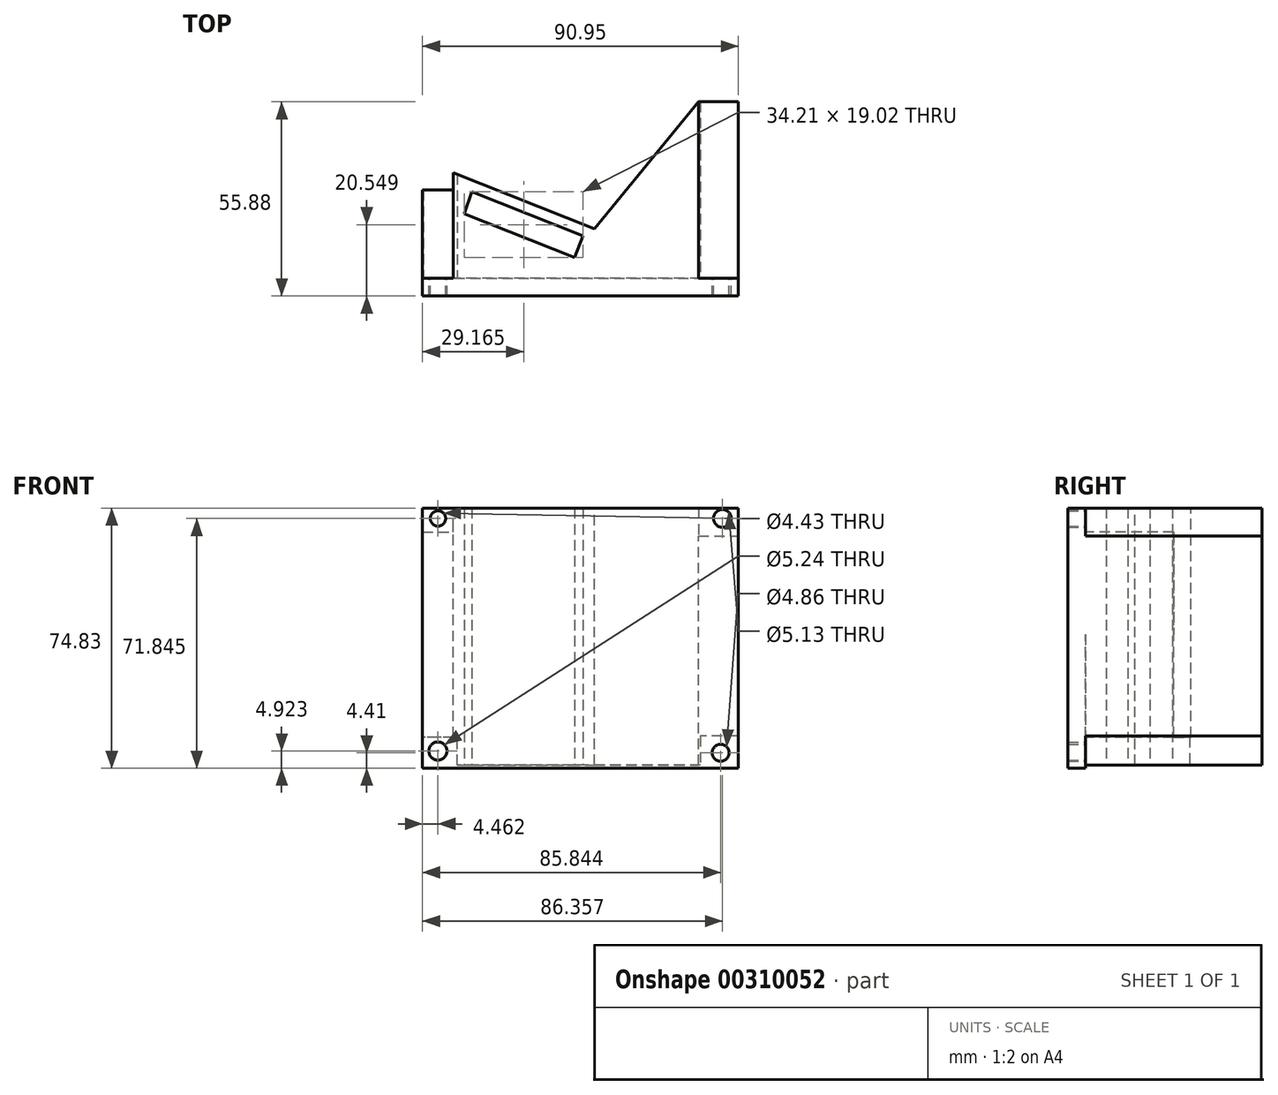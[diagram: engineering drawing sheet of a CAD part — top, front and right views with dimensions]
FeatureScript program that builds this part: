
annotation { "Feature Type Name" : "Feature", "Feature Type Description" : "" }
export const myFeature = defineFeature(function(context is Context, id is Id, definition is map)
    precondition{}
    {
        {
            var Q0;
            Q0=qCreatedBy(makeId("Front.planeOp"),FACE);
            var sketch = newSketch(context, id + "F0", { "sketchPlane" : qUnion([Q0])});
            skLineSegment(sketch, "E0.bottom", {"start": v(-36.84, 39.14) * mm, "end": v(54.1, 39.14) * mm});
            skLineSegment(sketch, "E0.top", {"start": v(-36.84, -35.69) * mm, "end": v(54.1, -35.69) * mm});
            skLineSegment(sketch, "E0.left", {"start": v(-36.84, 39.14) * mm, "end": v(-36.84, -35.69) * mm});
            skLineSegment(sketch, "E0.right", {"start": v(54.1, 39.14) * mm, "end": v(54.1, -35.69) * mm});
            skSolve(sketch);
        }
        {
            var Q0;
            Q0=makeQuery(id+"F0.imprint","IMPRINT",FACE,{"disambiguationData":[TD([[makeQuery(id+"F0.imprint","IMPRINT",EDGE,{"derivedFrom":sQuery(id+"F0.wireOp",EDGE,"E0.bottom")}),-1.0]])]});
            var sketch = newSketch(context, id + "F1", { "sketchPlane" : qUnion([Q0])});
            skLineSegment(sketch, "E1", {"start": v(-37.13, 32.23) * mm, "end": v(-27.92, 32.23) * mm});
            skLineSegment(sketch, "E2", {"start": v(-27.92, 32.23) * mm, "end": v(-27.92, 39.14) * mm});
            skLineSegment(sketch, "E3", {"start": v(-27.92, 39.14) * mm, "end": v(42.6, 39.14) * mm});
            skLineSegment(sketch, "E4", {"start": v(42.6, 39.14) * mm, "end": v(42.6, 31.08) * mm});
            skLineSegment(sketch, "E5", {"start": v(42.6, 31.08) * mm, "end": v(54.68, 31.08) * mm});
            skLineSegment(sketch, "E6", {"start": v(54.68, 31.08) * mm, "end": v(54.68, -26.48) * mm});
            skLineSegment(sketch, "E7", {"start": v(54.68, -26.48) * mm, "end": v(43.17, -26.48) * mm});
            skLineSegment(sketch, "E8", {"start": v(43.17, -26.48) * mm, "end": v(43.17, -34.82) * mm});
            skLineSegment(sketch, "E9", {"start": v(43.17, -34.82) * mm, "end": v(-26.77, -34.82) * mm});
            skLineSegment(sketch, "E10", {"start": v(-26.77, -34.82) * mm, "end": v(-26.77, -26.77) * mm});
            skLineSegment(sketch, "E11", {"start": v(-26.77, -26.77) * mm, "end": v(-36.55, -26.77) * mm});
            skLineSegment(sketch, "E12", {"start": v(-36.55, -26.77) * mm, "end": v(-37.13, 32.23) * mm});
            skSolve(sketch);
        }
        {
            var Q0;
            Q0=makeQuery(id+"F0.imprint","IMPRINT",FACE,{"disambiguationData":[TD([[makeQuery(id+"F0.imprint","IMPRINT",EDGE,{"derivedFrom":sQuery(id+"F0.wireOp",EDGE,"E0.bottom")}),-1.0]])]});
            extrude(context, id + "F2", {"entities" : qUnion([Q0]), "depth" : 5.08 * mm});
        }
        {
            var Q0;
            {var subQ7=sQuery(id+"F1.wireOp",EDGE,"E2");Q0=makeQuery(id+"F1.imprint","IMPRINT",FACE,{"disambiguationData":[TD([[makeQuery(id+"F1.imprint","IMPRINT",EDGE,{"derivedFrom":subQ7}),-1.0]])]});}
            extrude(context, id + "F3", {"entities" : qUnion([Q0]), "operationType" : NewBodyOperationType.ADD, "oppositeDirection" : true, "depth" : 50.8 * mm});
        }
        {
            var Q0;
            Q0=makeQuery(id+"F3.boolean.opBoolean","MERGE",FACE,{"derivedFrom":[makeQuery(id+"F2.opExtrude","SWEPT_FACE",FACE,{"disambiguationData":[OSD([sQuery(id+"F0.wireOp",EDGE,"E0.bottom")])]}),makeQuery(id+"F3.opExtrude","SWEPT_FACE",FACE,{"disambiguationData":[OSD([sQuery(id+"F1.wireOp",EDGE,"E3")])]})]});
            var sketch = newSketch(context, id + "F4", { "sketchPlane" : qUnion([Q0])});
            skLineSegment(sketch, "E13", {"start": v(-27.92, 30.39) * mm, "end": v(12.66, 14.23) * mm});
            skLineSegment(sketch, "E14", {"start": v(12.66, 14.23) * mm, "end": v(42.6, 50.8) * mm});
            skSolve(sketch);
        }
        {
            var Q0;
            {var subQ0=sQuery(id+"F4.wireOp",EDGE,"E13");Q0=makeQuery(id+"F4.imprint","IMPRINT",FACE,{"disambiguationData":[TD([[makeQuery(id+"F4.imprint","IMPRINT",EDGE,{"derivedFrom":subQ0}),1.0]])]});}
            extrude(context, id + "F5", {"entities" : qUnion([Q0]), "operationType" : NewBodyOperationType.REMOVE, "oppositeDirection" : true, "depth" : 76.2 * mm});
        }
        {
            var Q0;
            {var subQ0=sQuery(id+"F1.wireOp",EDGE,"E12");var subQ1=sQuery(id+"F1.wireOp",EDGE,"E11");var subQ2=sQuery(id+"F1.wireOp",EDGE,"E1");var subQ3=sQuery(id+"F0.wireOp",EDGE,"E0.left");var subQ4=sQuery(id+"F1.wireOp",EDGE,"E3");var subQ5=sQuery(id+"F1.wireOp",EDGE,"E2");Q0=makeQuery(id+"F5.boolean.opBoolean","SPLIT",FACE,{"disambiguationData":[TD([makeQuery(id+"F2.opExtrude","SWEPT_FACE",FACE,{"disambiguationData":[OSD([subQ3])]})])],"derivedFrom":makeQuery(id+"F3.opExtrude","CAP_FACE",FACE,{"disambiguationData":[OSD([subQ3,sQuery(id+"F0.wireOp",EDGE,"E0.right"),subQ2,subQ5,subQ4,sQuery(id+"F1.wireOp",EDGE,"E4"),sQuery(id+"F1.wireOp",EDGE,"E5"),sQuery(id+"F1.wireOp",EDGE,"E7"),sQuery(id+"F1.wireOp",EDGE,"E8"),sQuery(id+"F1.wireOp",EDGE,"E9"),sQuery(id+"F1.wireOp",EDGE,"E10"),subQ1,subQ0])],"isStart":false})});}
            extrude(context, id + "F6", {"entities" : qUnion([Q0]), "operationType" : NewBodyOperationType.REMOVE, "oppositeDirection" : true, "depth" : 25.4 * mm});
        }
        {
            var Q0;
            Q0=makeQuery(id+"F3.opExtrude","SWEPT_FACE",FACE,{"disambiguationData":[OSD([sQuery(id+"F1.wireOp",EDGE,"E9")])]});
            var sketch = newSketch(context, id + "F7", { "sketchPlane" : qUnion([Q0])});
            skLineSegment(sketch, "E15", {"start": v(-22.67, -24.98) * mm, "end": v(9.43, -12.2) * mm});
            skLineSegment(sketch, "E16", {"start": v(9.43, -12.2) * mm, "end": v(6.95, -5.96) * mm});
            skLineSegment(sketch, "E17", {"start": v(6.95, -5.96) * mm, "end": v(-24.78, -18.59) * mm});
            skPoint(sketch, "E17.endSnap0", {"position": v(-6.62, -18.59) * mm});
            skLineSegment(sketch, "E18", {"start": v(-24.78, -18.59) * mm, "end": v(-22.67, -24.98) * mm});
            skSolve(sketch);
        }
        {
            var Q0;
            Q0=makeQuery(id+"F7.imprint","IMPRINT",FACE,{"disambiguationData":[TD([[makeQuery(id+"F7.imprint","IMPRINT",EDGE,{"derivedFrom":sQuery(id+"F7.wireOp",EDGE,"E15")}),1.0]])]});
            extrude(context, id + "F8", {"entities" : qUnion([Q0]), "operationType" : NewBodyOperationType.REMOVE, "oppositeDirection" : true, "depth" : 101.6 * mm});
        }
        {
            var Q0;
            {var subQ0=sQuery(id+"F0.wireOp",EDGE,"E0.left");var subQ1=sQuery(id+"F0.wireOp",EDGE,"E0.bottom");Q0=makeQuery(id+"F3.boolean.opBoolean","SPLIT",FACE,{"disambiguationData":[TD([makeQuery(id+"F3.opExtrude","SWEPT_FACE",FACE,{"disambiguationData":[OSD([sQuery(id+"F1.wireOp",EDGE,"E1")])]})])],"derivedFrom":makeQuery(id+"F2.opExtrude","CAP_FACE",FACE,{"disambiguationData":[OSD([subQ1,sQuery(id+"F0.wireOp",EDGE,"E0.top"),subQ0,sQuery(id+"F0.wireOp",EDGE,"E0.right")])],"isStart":true})});}
            var sketch = newSketch(context, id + "F9", { "sketchPlane" : qUnion([Q0])});
            skCircle(sketch, "E19", {"center": v(32.38, 36.16) * mm, "radius": 2.21 * mm});
            skPoint(sketch, "E19.centerSnap0", {"position": v(32.38, 32.23) * mm});
            skCircle(sketch, "E20", {"center": v(32.38, -30.77) * mm, "radius": 2.62 * mm});
            skCircle(sketch, "E21", {"center": v(-49.52, 36.16) * mm, "radius": 2.56 * mm});
            skCircle(sketch, "E22", {"center": v(-49, -31.28) * mm, "radius": 2.43 * mm});
            skSolve(sketch);
        }
        {
            var Q0;
            Q0=makeQuery(id+"F9.imprint","IMPRINT",FACE,{"disambiguationData":[TD([[makeQuery(id+"F9.imprint","IMPRINT",EDGE,{"derivedFrom":sQuery(id+"F9.wireOp",EDGE,"E19")}),1.0]])]});
            var Q1;
            Q1=makeQuery(id+"F9.imprint","IMPRINT",FACE,{"disambiguationData":[TD([[makeQuery(id+"F9.imprint","IMPRINT",EDGE,{"derivedFrom":sQuery(id+"F9.wireOp",EDGE,"E20")}),1.0]])]});
            var Q2;
            Q2=makeQuery(id+"F9.imprint","IMPRINT",FACE,{"disambiguationData":[TD([[makeQuery(id+"F9.imprint","IMPRINT",EDGE,{"derivedFrom":sQuery(id+"F9.wireOp",EDGE,"E22")}),1.0]])]});
            var Q3;
            Q3=makeQuery(id+"F9.imprint","IMPRINT",FACE,{"disambiguationData":[TD([[makeQuery(id+"F9.imprint","IMPRINT",EDGE,{"derivedFrom":sQuery(id+"F9.wireOp",EDGE,"E21")}),1.0]])]});
            extrude(context, id + "F10", {"entities" : qUnion([Q0, Q1, Q2, Q3]), "operationType" : NewBodyOperationType.REMOVE, "oppositeDirection" : true, "depth" : 25.4 * mm});
        }
    });
